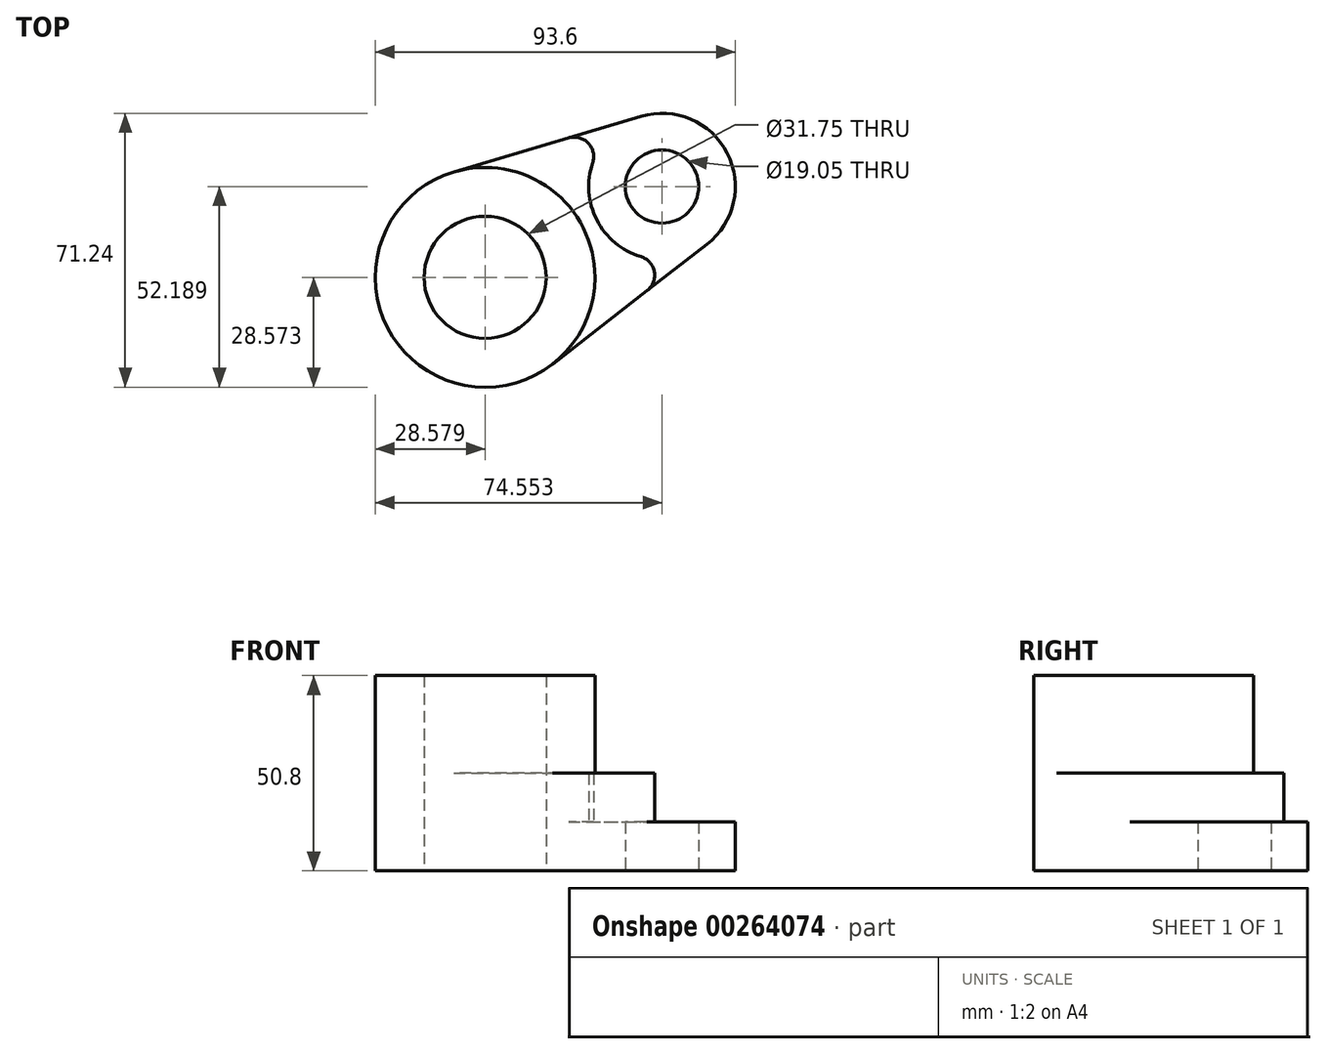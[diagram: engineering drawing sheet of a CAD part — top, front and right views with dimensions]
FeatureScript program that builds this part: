
annotation { "Feature Type Name" : "Feature", "Feature Type Description" : "" }
export const myFeature = defineFeature(function(context is Context, id is Id, definition is map)
    precondition{}
    {
        {
            var Q0;
            Q0=qCreatedBy(makeId("Top.planeOp"),FACE);
            var sketch = newSketch(context, id + "F0", { "sketchPlane" : qUnion([Q0])});
            skCircle(sketch, "E0", {"center": v(-40.54, -11.52) * mm, "radius": 28.58 * mm});
            skCircle(sketch, "E1", {"center": v(5.43, 12.1) * mm, "radius": 19.05 * mm});
            skCircle(sketch, "E2", {"center": v(-40.54, -11.52) * mm, "radius": 15.88 * mm});
            skCircle(sketch, "E3", {"center": v(5.43, 12.1) * mm, "radius": 9.53 * mm});
            skLineSegment(sketch, "E4", {"start": v(-48.7, 15.87) * mm, "end": v(0, 30.36) * mm});
            skLineSegment(sketch, "E5", {"start": v(-23.02, -34.1) * mm, "end": v(17.11, -2.95) * mm});
            skSolve(sketch);
        }
        {
            var Q0;
            Q0=makeQuery(id+"F0.imprint","IMPRINT",FACE,{"disambiguationData":[TD([[makeQuery(id+"F0.imprint","IMPRINT",EDGE,{"derivedFrom":sQuery(id+"F0.wireOp",EDGE,"E2")}),-1.0]])]});
            extrude(context, id + "F1", {"entities" : qUnion([Q0]), "depth" : 50.8 * mm});
        }
        {
            var Q0;
            {var subQ0=sQuery(id+"F0.wireOp",EDGE,"E4");Q0=makeQuery(id+"F0.imprint","IMPRINT",FACE,{"disambiguationData":[TD([[makeQuery(id+"F0.imprint","IMPRINT",EDGE,{"derivedFrom":subQ0}),-1.0]])]});}
            extrude(context, id + "F2", {"entities" : qUnion([Q0]), "operationType" : NewBodyOperationType.ADD, "depth" : 25.4 * mm});
        }
        {
            var Q0;
            Q0=makeQuery(id+"F0.imprint","IMPRINT",FACE,{"disambiguationData":[TD([[makeQuery(id+"F0.imprint","IMPRINT",EDGE,{"derivedFrom":sQuery(id+"F0.wireOp",EDGE,"E3")}),-1.0]])]});
            extrude(context, id + "F3", {"entities" : qUnion([Q0]), "operationType" : NewBodyOperationType.ADD, "depth" : 12.7 * mm});
        }
        {
            var Q0;
            {var subQ0=sQuery(id+"F0.wireOp",EDGE,"E1");var subQ1=sQuery(id+"F0.wireOp",EDGE,"E5");Q0=makeQuery(id+"F3.boolean.opBoolean","SPLIT",EDGE,{"disambiguationData":[topologyDisambiguationEdgeConnected([makeQuery(id+"F2.opExtrude","SWEPT_FACE",FACE,{"disambiguationData":[OSD([subQ0])]})])],"derivedFrom":makeQuery(id+"F2.opExtrude","SWEPT_EDGE",EDGE,{"disambiguationData":[OSD([subQ0,subQ1])]})});}
            var Q1;
            {var subQ0=sQuery(id+"F0.wireOp",EDGE,"E1");var subQ1=sQuery(id+"F0.wireOp",EDGE,"E4");Q1=makeQuery(id+"F3.boolean.opBoolean","SPLIT",EDGE,{"disambiguationData":[topologyDisambiguationEdgeConnected([makeQuery(id+"F2.opExtrude","SWEPT_FACE",FACE,{"disambiguationData":[OSD([subQ0])]})])],"derivedFrom":makeQuery(id+"F2.opExtrude","SWEPT_EDGE",EDGE,{"disambiguationData":[OSD([subQ0,subQ1])]})});}
            fillet(context, id + "F4", {"entities" : qUnion([Q0, Q1]), "radius" : 5.08 * mm, "tangentPropagation" : true, "allowEdgeOverflow" : false});
        }
    });
